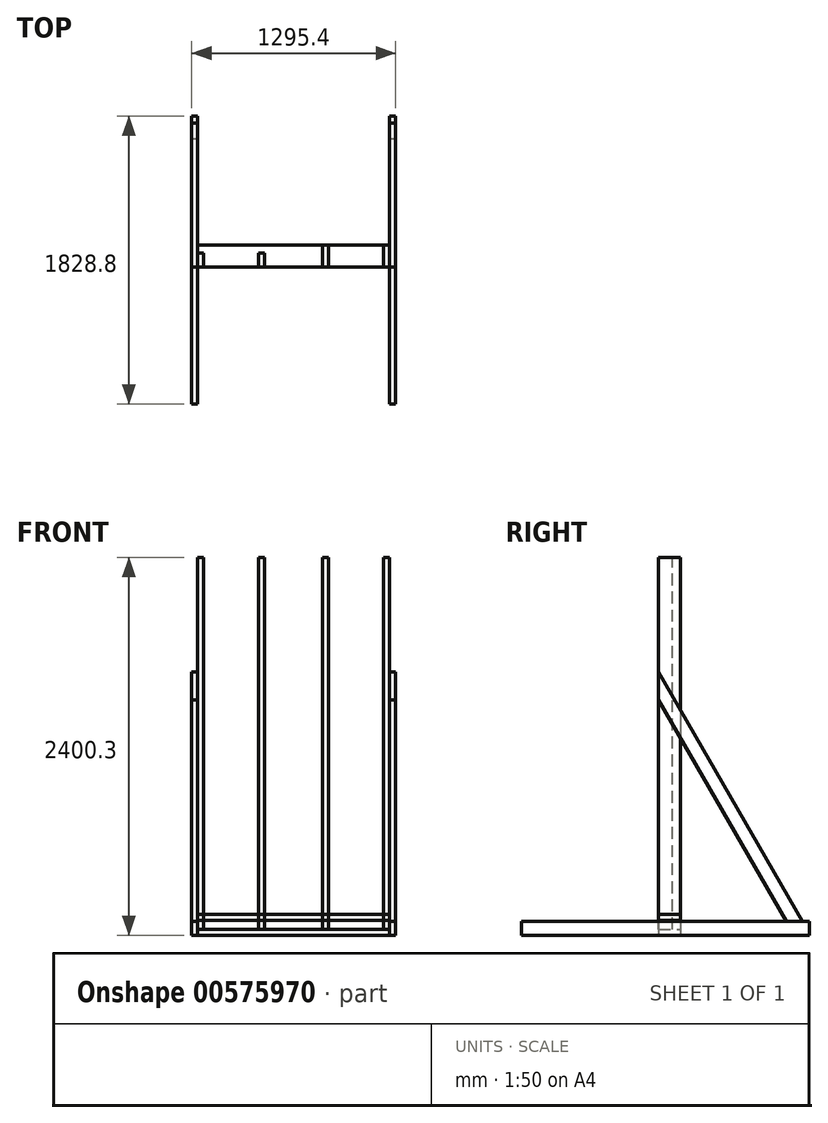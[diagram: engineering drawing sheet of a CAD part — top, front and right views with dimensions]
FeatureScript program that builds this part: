
annotation { "Feature Type Name" : "Feature", "Feature Type Description" : "" }
export const myFeature = defineFeature(function(context is Context, id is Id, definition is map)
    precondition{}
    {
        {
            var Q0;
            Q0=qCreatedBy(makeId("Front.planeOp"),FACE);
            var sketch = newSketch(context, id + "F0", { "sketchPlane" : qUnion([Q0])});
            skLineSegment(sketch, "E0.bottom", {"start": v(0, 0) * mm, "end": v(38.1, 0) * mm});
            skLineSegment(sketch, "E0.top", {"start": v(0, 2362.2) * mm, "end": v(38.1, 2362.2) * mm});
            skLineSegment(sketch, "E0.left", {"start": v(0, 0) * mm, "end": v(0, 2362.2) * mm});
            skLineSegment(sketch, "E0.right", {"start": v(38.1, 0) * mm, "end": v(38.1, 2362.2) * mm});
            skSolve(sketch);
        }
        {
            var Q0;
            Q0=qSketchRegion(id+"F0",true);
            extrude(context, id + "F1", {"entities" : qUnion([Q0]), "depth" : 88.9 * mm, "offsetDistance" : 25.4 * mm});
        }
        {
            var Q0;
            Q0=makeQuery(id+"F1.opExtrude","SWEPT_BODY",BODY,{"disambiguationData":[OSD([sQuery(id+"F0.wireOp",EDGE,"E0.bottom"),sQuery(id+"F0.wireOp",EDGE,"E0.top"),sQuery(id+"F0.wireOp",EDGE,"E0.left"),sQuery(id+"F0.wireOp",EDGE,"E0.right")])]});
            transform(context, id + "F2", {"entities" : qUnion([Q0]), "transformType" : TransformType.TRANSLATION_3D, "dx" : 387.35 * mm, "dy" : 0 * mm, "dz" : 0 * mm, "makeCopy" : true});
        }
        {
            var Q0;
            Q0=qCreatedBy(makeId("Front.planeOp"),FACE);
            var sketch = newSketch(context, id + "F3", { "sketchPlane" : qUnion([Q0])});
            skLineSegment(sketch, "E1.bottom", {"start": v(0, 0) * mm, "end": v(1219.2, 0) * mm});
            skLineSegment(sketch, "E1.top", {"start": v(0, -38.1) * mm, "end": v(1219.2, -38.1) * mm});
            skLineSegment(sketch, "E1.left", {"start": v(0, 0) * mm, "end": v(0, -38.1) * mm});
            skLineSegment(sketch, "E1.right", {"start": v(1219.2, 0) * mm, "end": v(1219.2, -38.1) * mm});
            skSolve(sketch);
        }
        {
            var Q0;
            Q0=qSketchRegion(id+"F3",true);
            extrude(context, id + "F4", {"entities" : qUnion([Q0]), "depth" : 88.9 * mm, "offsetDistance" : 25.4 * mm, "hasSecondDirection" : true, "secondDirectionOppositeDirection" : true, "secondDirectionDepth" : 50.8 * mm});
        }
        {
            var Q0;
            Q0=makeQuery(id+"F4.opExtrude","SWEPT_BODY",BODY,{"disambiguationData":[OSD([sQuery(id+"F3.wireOp",EDGE,"E1.bottom"),sQuery(id+"F3.wireOp",EDGE,"E1.top"),sQuery(id+"F3.wireOp",EDGE,"E1.left"),sQuery(id+"F3.wireOp",EDGE,"E1.right")])]});
            transform(context, id + "F5", {"entities" : qUnion([Q0]), "transformType" : TransformType.TRANSLATION_3D, "dx" : 0 * mm, "dy" : 0 * mm, "dz" : ((8 * 12) - 1.5) * mm, "makeCopy" : true});
        }
        {
            var Q0;
            Q0=makeQuery(id+"F4.opExtrude","SWEPT_FACE",FACE,{"disambiguationData":[OSD([sQuery(id+"F3.wireOp",EDGE,"E1.left")])]});
            var sketch = newSketch(context, id + "F6", { "sketchPlane" : qUnion([Q0])});
            skLineSegment(sketch, "E2.bottom", {"start": v(958.85, 50.8) * mm, "end": v(-869.95, 50.8) * mm});
            skLineSegment(sketch, "E2.top", {"start": v(958.85, -38.1) * mm, "end": v(-869.95, -38.1) * mm});
            skLineSegment(sketch, "E2.left", {"start": v(958.85, 50.8) * mm, "end": v(958.85, -38.1) * mm});
            skLineSegment(sketch, "E2.right", {"start": v(-869.95, 50.8) * mm, "end": v(-869.95, -38.1) * mm});
            skSolve(sketch);
        }
        {
            var Q0;
            Q0=qSketchRegion(id+"F6",true);
            extrude(context, id + "F7", {"entities" : qUnion([Q0]), "depth" : 38.1 * mm, "offsetDistance" : 25.4 * mm});
        }
        {
            var Q0;
            Q0=makeQuery(id+"F7.opExtrude","SWEPT_BODY",BODY,{"disambiguationData":[OSD([sQuery(id+"F6.wireOp",EDGE,"E2.bottom"),sQuery(id+"F6.wireOp",EDGE,"E2.top"),sQuery(id+"F6.wireOp",EDGE,"E2.left"),sQuery(id+"F6.wireOp",EDGE,"E2.right")])]});
            transform(context, id + "F8", {"entities" : qUnion([Q0]), "transformType" : TransformType.TRANSLATION_3D, "dx" : 1257.3 * mm, "dy" : 0 * mm, "dz" : 0 * mm, "makeCopy" : true});
        }
        {
            var Q0;
            Q0=makeQuery(id+"F2.opPattern","COPY",FACE,{"derivedFrom":makeQuery(id+"F1.opExtrude","SWEPT_FACE",FACE,{"disambiguationData":[OSD([sQuery(id+"F0.wireOp",EDGE,"E0.right")])]}),"instanceName":"1"});
            cPlane(context, id + "F9", {"entities" : qUnion([Q0]), "cplaneType" : CPlaneType.OFFSET, "offset" : 368.3 * mm, "width" : 152.4 * mm, "height" : 152.4 * mm});
        }
        {
            var Q0;
            Q0=qCreatedBy(id+"F9.planeOp",FACE);
            var sketch = newSketch(context, id + "F10", { "sketchPlane" : qUnion([Q0])});
            skLineSegment(sketch, "E3.bottom", {"start": v(-88.9, 2362.2) * mm, "end": v(50.8, 2362.2) * mm});
            skLineSegment(sketch, "E3.top", {"start": v(-88.9, 0) * mm, "end": v(50.8, 0) * mm});
            skLineSegment(sketch, "E3.left", {"start": v(-88.9, 2362.2) * mm, "end": v(-88.9, 0) * mm});
            skLineSegment(sketch, "E3.right", {"start": v(50.8, 2362.2) * mm, "end": v(50.8, 0) * mm});
            skSolve(sketch);
        }
        {
            var Q0;
            Q0 = qSketchRegion(id + "F10", true);
            extrude(context, id + "F11", {"entities" : qUnion([Q0]), "depth" : 38.1 * mm, "offsetDistance" : 25.4 * mm});
        }
        {
            var Q0;
            Q0=makeQuery(id+"F11.opExtrude","SWEPT_BODY",BODY,{"disambiguationData":[OSD([sQuery(id+"F10.wireOp",EDGE,"E3.bottom"),sQuery(id+"F10.wireOp",EDGE,"E3.top"),sQuery(id+"F10.wireOp",EDGE,"E3.left"),sQuery(id+"F10.wireOp",EDGE,"E3.right")])]});
            transform(context, id + "F12", {"entities" : qUnion([Q0]), "transformType" : TransformType.TRANSLATION_3D, "dx" : 387.35 * mm, "dy" : 0 * mm, "dz" : 0 * mm, "makeCopy" : true});
        }
        {
            var Q0;
            Q0=makeQuery(id+"F8.opPattern","COPY",FACE,{"derivedFrom":makeQuery(id+"F7.opExtrude","CAP_FACE",FACE,{"disambiguationData":[OSD([sQuery(id+"F6.wireOp",EDGE,"E2.bottom"),sQuery(id+"F6.wireOp",EDGE,"E2.top"),sQuery(id+"F6.wireOp",EDGE,"E2.left"),sQuery(id+"F6.wireOp",EDGE,"E2.right")])],"isStart":false}),"instanceName":"1"});
            var sketch = newSketch(context, id + "F13", { "sketchPlane" : qUnion([Q0])});
            skLineSegment(sketch, "E4", {"start": v(-825.5, 50.8) * mm, "end": v(0, 1480.6) * mm});
            skLineSegment(sketch, "E5", {"start": v(0, 1480.6) * mm, "end": v(0, 1302.8) * mm});
            skLineSegment(sketch, "E6", {"start": v(0, 1302.8) * mm, "end": v(-722.85, 50.8) * mm});
            skLineSegment(sketch, "E7", {"start": v(-825.5, 50.8) * mm, "end": v(-722.85, 50.8) * mm});
            skLineSegment(sketch, "E8", {"start": v(0, 1480.6) * mm, "end": v(88.9, 1634.59) * mm});
            skLineSegment(sketch, "E9", {"start": v(0, 1302.8) * mm, "end": v(88.9, 1456.79) * mm});
            skLineSegment(sketch, "E10", {"start": v(88.9, 1634.59) * mm, "end": v(88.9, 1456.79) * mm});
            skSolve(sketch);
        }
        {
            var Q0;
            Q0=qSketchRegion(id+"F13",true);
            extrude(context, id + "F14", {"entities" : qUnion([Q0]), "oppositeDirection" : true, "depth" : 38.1 * mm, "offsetDistance" : 25.4 * mm});
        }
        {
            var Q0;
            Q0=makeQuery(id+"F14.opExtrude","SWEPT_BODY",BODY,{"disambiguationData":[OSD([sQuery(id+"F13.wireOp",EDGE,"E4"),sQuery(id+"F13.wireOp",EDGE,"E5"),sQuery(id+"F13.wireOp",EDGE,"E6"),sQuery(id+"F13.wireOp",EDGE,"1W0fkmu6-52x2-68E4-ANrA-ky8dyzSj9vcL")])]});
            transform(context, id + "F15", {"entities" : qUnion([Q0]), "transformType" : TransformType.TRANSLATION_3D, "dx" : -1257.3 * mm, "dy" : 0 * mm, "dz" : 0 * mm, "makeCopy" : true});
        }
    });
